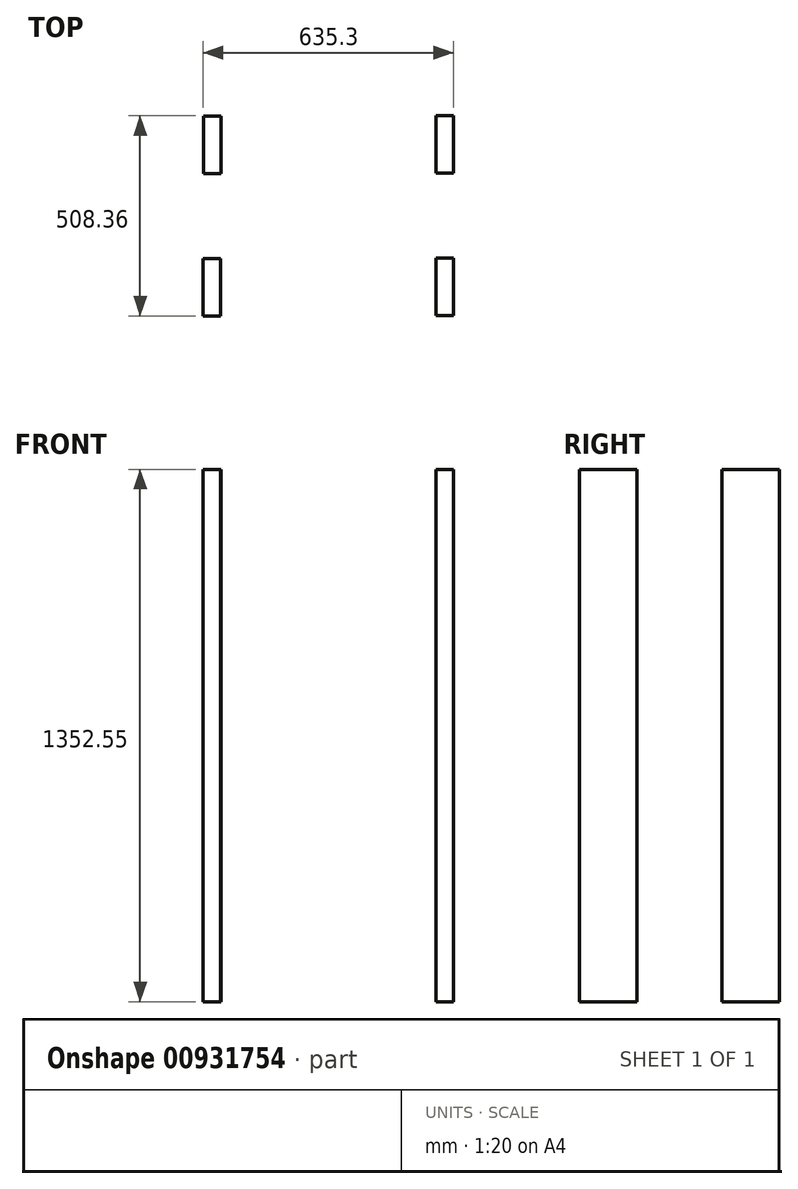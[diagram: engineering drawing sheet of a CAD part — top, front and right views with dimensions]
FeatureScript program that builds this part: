
annotation { "Feature Type Name" : "Feature", "Feature Type Description" : "" }
export const myFeature = defineFeature(function(context is Context, id is Id, definition is map)
    precondition{}
    {
        {
            var Q0;
            Q0=qCreatedBy(makeId("Top.planeOp"),FACE);
            var sketch = newSketch(context, id + "F0", { "sketchPlane" : qUnion([Q0])});
            skLineSegment(sketch, "E0.bottom", {"start": v(-52.66, 145.57) * mm, "end": v(-8.2, 145.57) * mm});
            skLineSegment(sketch, "E0.top", {"start": v(-52.66, -0.48) * mm, "end": v(-8.2, -0.48) * mm});
            skLineSegment(sketch, "E0.left", {"start": v(-52.66, 145.57) * mm, "end": v(-52.66, -0.48) * mm});
            skLineSegment(sketch, "E0.right", {"start": v(-8.2, 145.57) * mm, "end": v(-8.2, -0.48) * mm});
            skSolve(sketch);
        }
        {
            var Q0;
            Q0=makeQuery(id+"F0.imprint","IMPRINT",FACE,{"disambiguationData":[TD([[makeQuery(id+"F0.imprint","IMPRINT",EDGE,{"derivedFrom":sQuery(id+"F0.wireOp",EDGE,"E0.bottom")}),-1.0]])]});
            extrude(context, id + "F1", {"entities" : qUnion([Q0]), "depth" : 1371.6 * mm - 19.05 * mm, "offsetDistance" : 25.4 * mm});
        }
        {
            var Q0;
            Q0=qCreatedBy(makeId("Top.planeOp"),FACE);
            var sketch = newSketch(context, id + "F2", { "sketchPlane" : qUnion([Q0])});
            skLineSegment(sketch, "E1.bottom", {"start": v(537.9, 145.93) * mm, "end": v(582.34, 145.93) * mm});
            skLineSegment(sketch, "E1.top", {"start": v(537.9, -0.12) * mm, "end": v(582.34, -0.12) * mm});
            skLineSegment(sketch, "E1.left", {"start": v(537.9, 145.93) * mm, "end": v(537.9, -0.12) * mm});
            skLineSegment(sketch, "E1.right", {"start": v(582.34, 145.93) * mm, "end": v(582.34, -0.12) * mm});
            skSolve(sketch);
        }
        {
            var Q0;
            Q0=makeQuery(id+"F2.imprint","IMPRINT",FACE,{"disambiguationData":[TD([[makeQuery(id+"F2.imprint","IMPRINT",EDGE,{"derivedFrom":sQuery(id+"F2.wireOp",EDGE,"E1.bottom")}),-1.0]])]});
            extrude(context, id + "F3", {"entities" : qUnion([Q0]), "depth" : 1371.6 * mm - 19.05 * mm, "offsetDistance" : 25.4 * mm});
        }
        {
            var Q0;
            Q0=qCreatedBy(makeId("Top.planeOp"),FACE);
            var sketch = newSketch(context, id + "F4", { "sketchPlane" : qUnion([Q0])});
            skLineSegment(sketch, "E2.bottom", {"start": v(-8.51, -216.38) * mm, "end": v(-52.96, -216.38) * mm});
            skLineSegment(sketch, "E2.top", {"start": v(-8.51, -362.43) * mm, "end": v(-52.96, -362.43) * mm});
            skLineSegment(sketch, "E2.left", {"start": v(-8.51, -216.38) * mm, "end": v(-8.51, -362.43) * mm});
            skLineSegment(sketch, "E2.right", {"start": v(-52.96, -216.38) * mm, "end": v(-52.96, -362.43) * mm});
            skSolve(sketch);
        }
        {
            var Q0;
            Q0=makeQuery(id+"F4.imprint","IMPRINT",FACE,{"disambiguationData":[TD([[makeQuery(id+"F4.imprint","IMPRINT",EDGE,{"derivedFrom":sQuery(id+"F4.wireOp",EDGE,"E2.bottom")}),1.0]])]});
            extrude(context, id + "F5", {"entities" : qUnion([Q0]), "depth" : 1371.6 * mm - 19.05 * mm, "offsetDistance" : 25.4 * mm});
        }
        {
            var Q0;
            Q0=qCreatedBy(makeId("Top.planeOp"),FACE);
            var sketch = newSketch(context, id + "F6", { "sketchPlane" : qUnion([Q0])});
            skLineSegment(sketch, "E3.bottom", {"start": v(582.34, -216.02) * mm, "end": v(537.9, -216.02) * mm});
            skLineSegment(sketch, "E3.top", {"start": v(582.34, -362.07) * mm, "end": v(537.9, -362.07) * mm});
            skLineSegment(sketch, "E3.left", {"start": v(582.34, -216.02) * mm, "end": v(582.34, -362.07) * mm});
            skLineSegment(sketch, "E3.right", {"start": v(537.9, -216.02) * mm, "end": v(537.9, -362.07) * mm});
            skSolve(sketch);
        }
        {
            var Q0;
            Q0=makeQuery(id+"F6.imprint","IMPRINT",FACE,{"disambiguationData":[TD([[makeQuery(id+"F6.imprint","IMPRINT",EDGE,{"derivedFrom":sQuery(id+"F6.wireOp",EDGE,"E3.bottom")}),1.0]])]});
            extrude(context, id + "F7", {"entities" : qUnion([Q0]), "depth" : 1371.6 * mm - 19.05 * mm, "offsetDistance" : 25.4 * mm});
        }
    });
